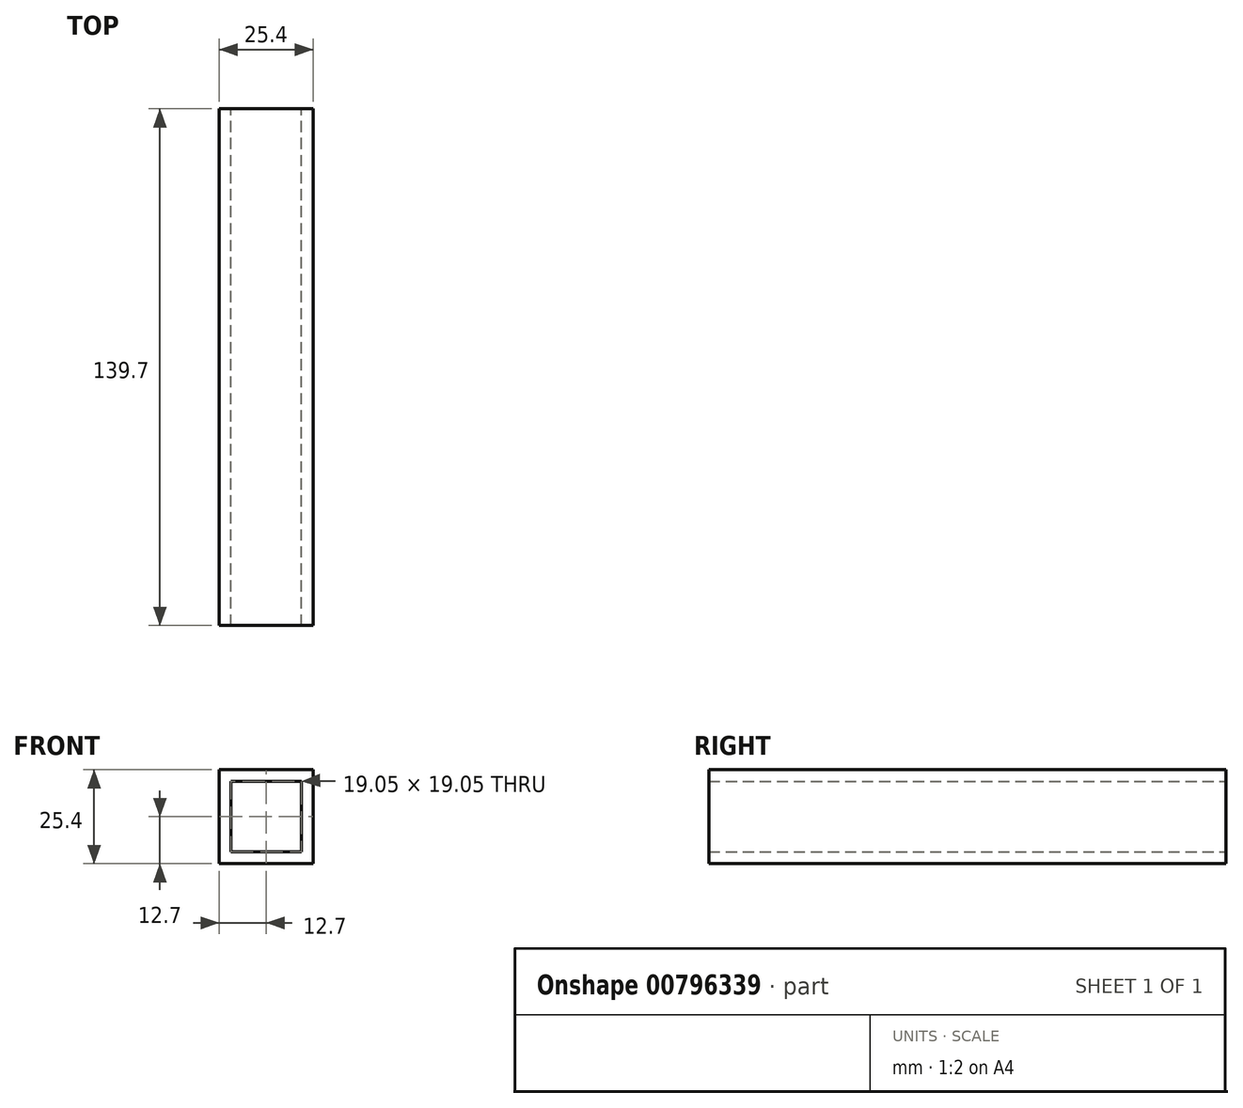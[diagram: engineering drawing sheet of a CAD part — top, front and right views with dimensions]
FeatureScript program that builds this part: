
annotation { "Feature Type Name" : "Feature", "Feature Type Description" : "" }
export const myFeature = defineFeature(function(context is Context, id is Id, definition is map)
    precondition{}
    {
        {
            var Q0;
            Q0=qCreatedBy(makeId("Front.planeOp"),FACE);
            var sketch = newSketch(context, id + "F0", { "sketchPlane" : qUnion([Q0])});
            skLineSegment(sketch, "E0.bottom", {"start": v(-12.7, 12.7) * mm, "end": v(12.7, 12.7) * mm});
            skLineSegment(sketch, "E0.top", {"start": v(-12.7, -12.7) * mm, "end": v(12.7, -12.7) * mm});
            skLineSegment(sketch, "E0.left", {"start": v(-12.7, 12.7) * mm, "end": v(-12.7, -12.7) * mm});
            skLineSegment(sketch, "E0.right", {"start": v(12.7, 12.7) * mm, "end": v(12.7, -12.7) * mm});
            skPoint(sketch, "E0.middle", {"position": v(0, 0) * mm});
            skLineSegment(sketch, "E1.bottom", {"start": v(-9.52, 9.52) * mm, "end": v(9.52, 9.52) * mm});
            skLineSegment(sketch, "E1.top", {"start": v(-9.53, -9.52) * mm, "end": v(9.52, -9.52) * mm});
            skLineSegment(sketch, "E1.left", {"start": v(-9.52, 9.52) * mm, "end": v(-9.53, -9.52) * mm});
            skLineSegment(sketch, "E1.right", {"start": v(9.53, 9.52) * mm, "end": v(9.52, -9.52) * mm});
            skSolve(sketch);
        }
        {
            var Q0;
            Q0=makeQuery(id+"F0.imprint","IMPRINT",FACE,{"disambiguationData":[TD([[makeQuery(id+"F0.imprint","IMPRINT",EDGE,{"derivedFrom":sQuery(id+"F0.wireOp",EDGE,"E0.bottom")}),-1.0]])]});
            extrude(context, id + "F1", {"entities" : qUnion([Q0]), "depth" : 139.7 * mm, "offsetDistance" : 25.4 * mm});
        }
    });
